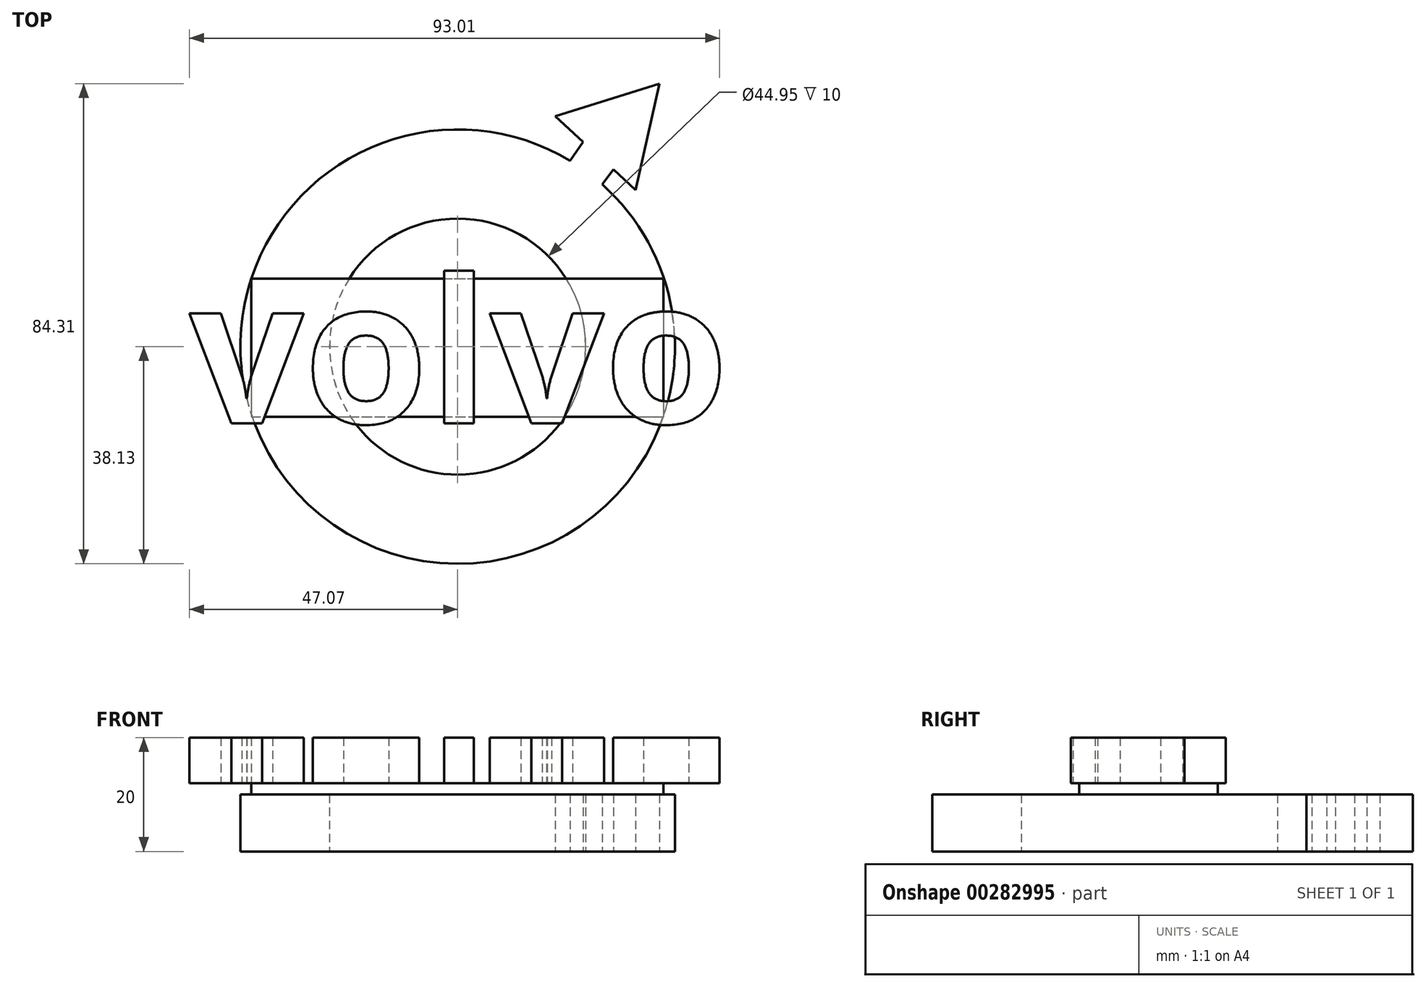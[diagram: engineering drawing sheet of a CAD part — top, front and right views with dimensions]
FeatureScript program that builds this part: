
annotation { "Feature Type Name" : "Feature", "Feature Type Description" : "" }
export const myFeature = defineFeature(function(context is Context, id is Id, definition is map)
    precondition{}
    {
        {
            var Q0;
            Q0=qCreatedBy(makeId("Top.planeOp"),FACE);
            var sketch = newSketch(context, id + "F0", { "sketchPlane" : qUnion([Q0])});
            skCircle(sketch, "E0", {"center": v(0, 0) * mm, "radius": 38.13 * mm});
            skCircle(sketch, "E1", {"center": v(0, 0) * mm, "radius": 22.48 * mm});
            skLineSegment(sketch, "E2", {"start": v(25.34, 28.48) * mm, "end": v(29.66, 34.15) * mm});
            skLineSegment(sketch, "E3", {"start": v(19.7, 32.64) * mm, "end": v(23.79, 38.47) * mm});
            skLineSegment(sketch, "E4", {"start": v(17.14, 40.43) * mm, "end": v(31.24, 27.5) * mm});
            skLineSegment(sketch, "E5", {"start": v(17.14, 40.43) * mm, "end": v(35.38, 46.18) * mm});
            skLineSegment(sketch, "E6", {"start": v(35.38, 46.18) * mm, "end": v(31.24, 27.5) * mm});
            skText(sketch, "E7", { "text": "volvo", "fontName": "NotoSansCJKsc-Bold.otf"});
            const initialGuessF0  = {"E7": [0.08442, 0.0222, 1, 0, 0.02203]};
            skSetInitialGuess(sketch, initialGuessF0);
            skSolve(sketch);
        }
        {
            var Q0;
            Q0=makeQuery(id+"F0.imprint","IMPRINT",FACE,{"disambiguationData":[TD([[makeQuery(id+"F0.imprint","IMPRINT",EDGE,{"derivedFrom":sQuery(id+"F0.wireOp",EDGE,"E1")}),-1.0]])]});
            var Q1;
            {var subQ0=sQuery(id+"F0.wireOp",EDGE,"E5");Q1=makeQuery(id+"F0.imprint","IMPRINT",FACE,{"disambiguationData":[TD([[makeQuery(id+"F0.imprint","IMPRINT",EDGE,{"derivedFrom":subQ0}),-1.0]])]});}
            var Q2;
            {var subQ0=sQuery(id+"F0.wireOp",EDGE,"E2");var subQ1=sQuery(id+"F0.wireOp",EDGE,"E0");var subQ2=makeQuery(id+"F0.imprint","INTERSECT",VERTEX,{"derivedFrom":[subQ1,subQ0]});Q2=makeQuery(id+"F0.imprint","IMPRINT",FACE,{"disambiguationData":[TD([[makeQuery(id+"F0.imprint","IMPRINT",EDGE,{"disambiguationData":[TD([[subQ2,-1.0]])],"derivedFrom":subQ1}),-1.0]])]});}
            extrude(context, id + "F1", {"entities" : qUnion([Q0, Q1, Q2]), "depth" : 10 * mm});
        }
        {
            var Q0;
            Q0=makeQuery(id+"F1.opExtrude","CAP_FACE",FACE,{"disambiguationData":[OSD([sQuery(id+"F0.wireOp",EDGE,"E0"),sQuery(id+"F0.wireOp",EDGE,"E1"),sQuery(id+"F0.wireOp",EDGE,"E2"),sQuery(id+"F0.wireOp",EDGE,"E3"),sQuery(id+"F0.wireOp",EDGE,"E4"),sQuery(id+"F0.wireOp",EDGE,"E5"),sQuery(id+"F0.wireOp",EDGE,"E6")])],"isStart":false});
            var sketch = newSketch(context, id + "F2", { "sketchPlane" : qUnion([Q0])});
            skLineSegment(sketch, "E8.bottom", {"start": v(-36.2, 11.95) * mm, "end": v(36.08, 11.95) * mm});
            skLineSegment(sketch, "E8.top", {"start": v(-36.2, -12.32) * mm, "end": v(36.08, -12.32) * mm});
            skLineSegment(sketch, "E8.left", {"start": v(-36.2, 11.95) * mm, "end": v(-36.2, -12.32) * mm});
            skLineSegment(sketch, "E8.right", {"start": v(36.08, 11.95) * mm, "end": v(36.08, -12.32) * mm});
            skSolve(sketch);
        }
        {
            var Q0;
            {var subQ0=sQuery(id+"F2.wireOp",EDGE,"E8.bottom");var subQ1=makeQuery(id+"F1.opExtrude","CAP_EDGE",EDGE,{"disambiguationData":[OSD([sQuery(id+"F0.wireOp",EDGE,"E1")])],"isStart":false});var subQ2=makeQuery(id+"F2.imprint","INTERSECT",VERTEX,{"disambiguationData":[OD(0.0)],"derivedFrom":[subQ1,subQ0]});Q0=makeQuery(id+"F2.imprint","IMPRINT",FACE,{"disambiguationData":[TD([[makeQuery(id+"F2.imprint","IMPRINT",EDGE,{"disambiguationData":[TD([[subQ2,-1.0]])],"derivedFrom":subQ0}),-1.0]])]});}
            var Q1;
            {var subQ0=sQuery(id+"F2.wireOp",EDGE,"E8.right");Q1=makeQuery(id+"F2.imprint","IMPRINT",FACE,{"disambiguationData":[TD([[makeQuery(id+"F2.imprint","IMPRINT",EDGE,{"derivedFrom":subQ0}),-1.0]])]});}
            var Q2;
            {var subQ2=makeQuery(id+"F1.opExtrude","CAP_EDGE",EDGE,{"disambiguationData":[OSD([sQuery(id+"F0.wireOp",EDGE,"E0")])],"isStart":false});var subQ5=sQuery(id+"F2.wireOp",EDGE,"E8.top");var subQ6=makeQuery(id+"F2.imprint","INTERSECT",VERTEX,{"derivedFrom":[subQ2,subQ5]});Q2=makeQuery(id+"F2.imprint","IMPRINT",FACE,{"disambiguationData":[TD([[makeQuery(id+"F2.imprint","IMPRINT",EDGE,{"disambiguationData":[TD([[subQ6,-1.0]])],"derivedFrom":subQ5}),1.0]])]});}
            var Q3;
            {var subQ0=sQuery(id+"F2.wireOp",EDGE,"E8.left");Q3=makeQuery(id+"F2.imprint","IMPRINT",FACE,{"disambiguationData":[TD([[makeQuery(id+"F2.imprint","IMPRINT",EDGE,{"derivedFrom":subQ0}),1.0]])]});}
            var Q4;
            {var subQ0=sQuery(id+"F2.wireOp",EDGE,"E8.bottom");var subQ1=makeQuery(id+"F1.opExtrude","CAP_EDGE",EDGE,{"disambiguationData":[OSD([sQuery(id+"F0.wireOp",EDGE,"E0")])],"isStart":false});var subQ2=makeQuery(id+"F2.imprint","INTERSECT",VERTEX,{"derivedFrom":[subQ1,subQ0]});Q4=makeQuery(id+"F2.imprint","IMPRINT",FACE,{"disambiguationData":[TD([[makeQuery(id+"F2.imprint","IMPRINT",EDGE,{"disambiguationData":[TD([[subQ2,1.0]])],"derivedFrom":subQ0}),-1.0]])]});}
            extrude(context, id + "F3", {"entities" : qUnion([Q0, Q1, Q2, Q3, Q4]), "operationType" : NewBodyOperationType.ADD, "depth" : 2 * mm});
        }
        {
            var Q0;
            Q0=makeQuery(id+"F3.opExtrude","CAP_FACE",FACE,{"disambiguationData":[OSD([sQuery(id+"F2.wireOp",EDGE,"E8.bottom"),sQuery(id+"F2.wireOp",EDGE,"E8.top"),sQuery(id+"F2.wireOp",EDGE,"E8.left"),sQuery(id+"F2.wireOp",EDGE,"E8.right")])],"isStart":false});
            var sketch = newSketch(context, id + "F4", { "sketchPlane" : qUnion([Q0])});
            skText(sketch, "E9", { "text": "volvo", "fontName": "OpenSans-Bold.ttf"});
            const initialGuessF4  = {"E9": [-0.04707, -0.01345, 1, 0, 0.0254]};
            skSetInitialGuess(sketch, initialGuessF4);
            skSolve(sketch);
        }
        {
            var Q0;
            Q0 = qSketchRegion(id + "F4", true);
            extrude(context, id + "F5", {"entities" : qUnion([Q0]), "operationType" : NewBodyOperationType.ADD, "depth" : 8 * mm});
        }
    });
